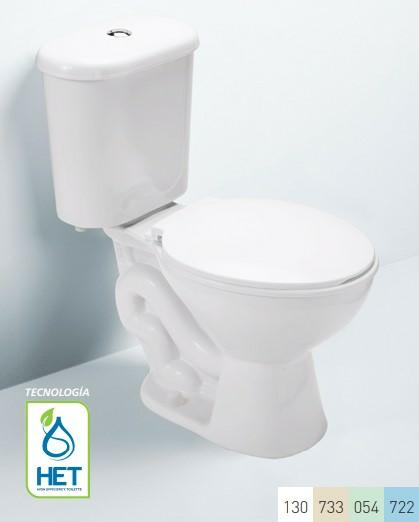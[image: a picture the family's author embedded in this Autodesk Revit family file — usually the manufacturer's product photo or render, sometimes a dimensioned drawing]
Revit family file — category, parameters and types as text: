
# Revit family: BRG-CMP-ACC_DISPENSADOR DE PAPEL CIRCULAR v03
name_source: partatom
category: Aparatos sanitarios
units: mm (PartAtom-declared; Revit-internal decimal feet)

## family parameters
Anfitrión = Muro
Compartido = No
Corte con vacíos al cargar = No
Cota de conector redondo = Diámetro de uso
Número OmniClass = 23.45.00.00
Punto de cálculo de habitación = No
Siempre vertical = Sí
Tipo de pieza = Normal
Título OmniClass = Sanitary, Laundry, and Cleaning Equipment

## types (1)
- DISPENSADOR DE PAPEL CIRCULAR
    Fabricante = BRIGGS
    Modelo = DISPENSADOR DE PAPEL CIRCULAR
    URL = https://www.briggs.com.ec
    _EDESA_ Alto en cm = 27.5
    _EDESA_ Ancho en cm = 27
    _EDESA_ Categoría = Productos > Complementos > Accesorios
    _EDESA_ Color = cromo
    _EDESA_ Descripción = Dispensador de papel higiénico para lugares de alto tráfico.
    _EDESA_ Garantía = 2 años
    _EDESA_ Marca = BRIGGS
    _EDESA_ Materiales = Acero Inoxidable S304
    _EDESA_ Nombre = DISPENSADOR DE PAPEL CIRCULAR
    _EDESA_ Productos incluídos = Tacos y tornillos
    _EDESA_ Profundidad en cm = 12.7
    _EDESA_ Página web = https://www.briggs.com.ec
    _EDESA_ Sku/código = SC0028593061CW
    _EDESA_ Tipo de instalación = A la pared
